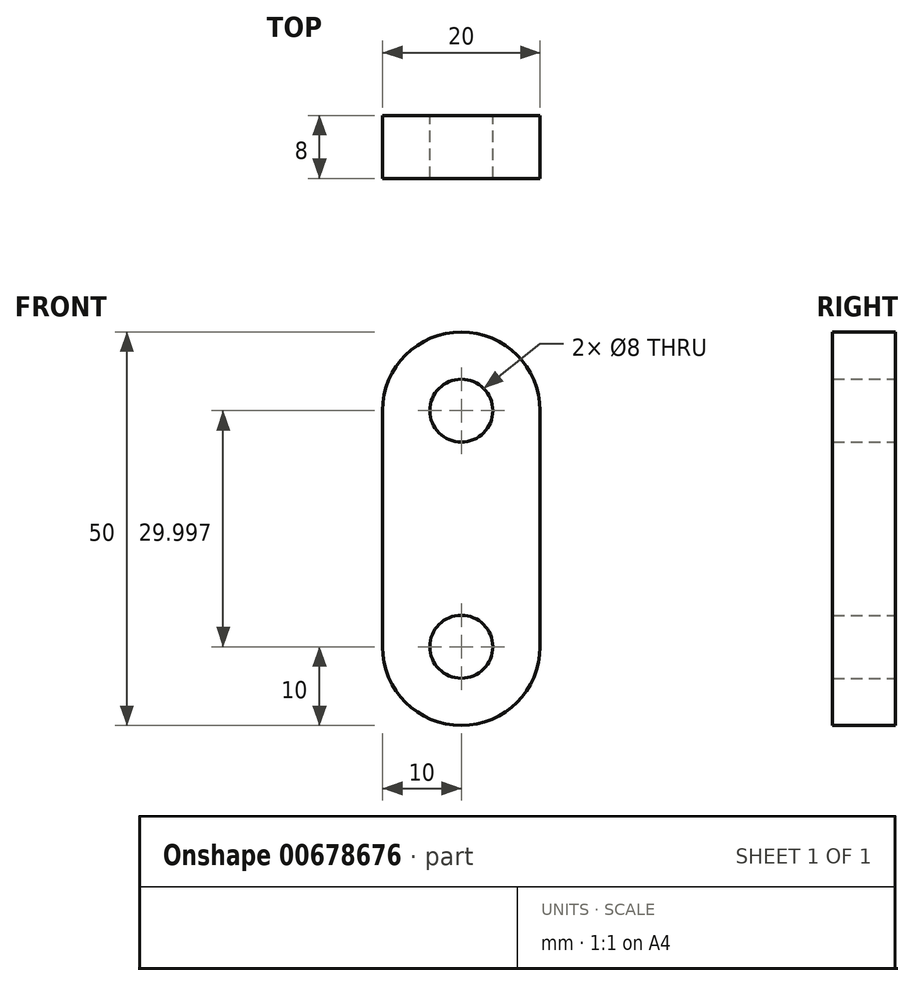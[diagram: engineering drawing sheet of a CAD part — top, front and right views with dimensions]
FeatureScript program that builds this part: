
annotation { "Feature Type Name" : "Feature", "Feature Type Description" : "" }
export const myFeature = defineFeature(function(context is Context, id is Id, definition is map)
    precondition{}
    {
        {
            var Q0;
            Q0=qCreatedBy(makeId("Front.planeOp"),FACE);
            var sketch = newSketch(context, id + "F0", { "sketchPlane" : qUnion([Q0])});
            skArc(sketch, "E0", {"start": v(-10, 0) * mm, "mid": v(0, -10) * mm, "end": v(10, 0) * mm});
            skCircle(sketch, "E1", {"center": v(0, 0) * mm, "radius": 4 * mm});
            skCircle(sketch, "E2", {"center": v(0, 30) * mm, "radius": 4 * mm});
            skArc(sketch, "E3", {"start": v(10, 30) * mm, "mid": v(0, 40) * mm, "end": v(-10, 30) * mm});
            skLineSegment(sketch, "E4", {"start": v(-10, 30) * mm, "end": v(-10, 0) * mm});
            skLineSegment(sketch, "E5", {"start": v(10, 0) * mm, "end": v(10, 30) * mm});
            skSolve(sketch);
        }
        {
            var Q0;
            Q0 = qSketchRegion(id + "F0", true);
            extrude(context, id + "F1", {"entities" : qUnion([Q0]), "depth" : 8 * mm, "offsetDistance" : 25.4 * mm});
        }
    });
